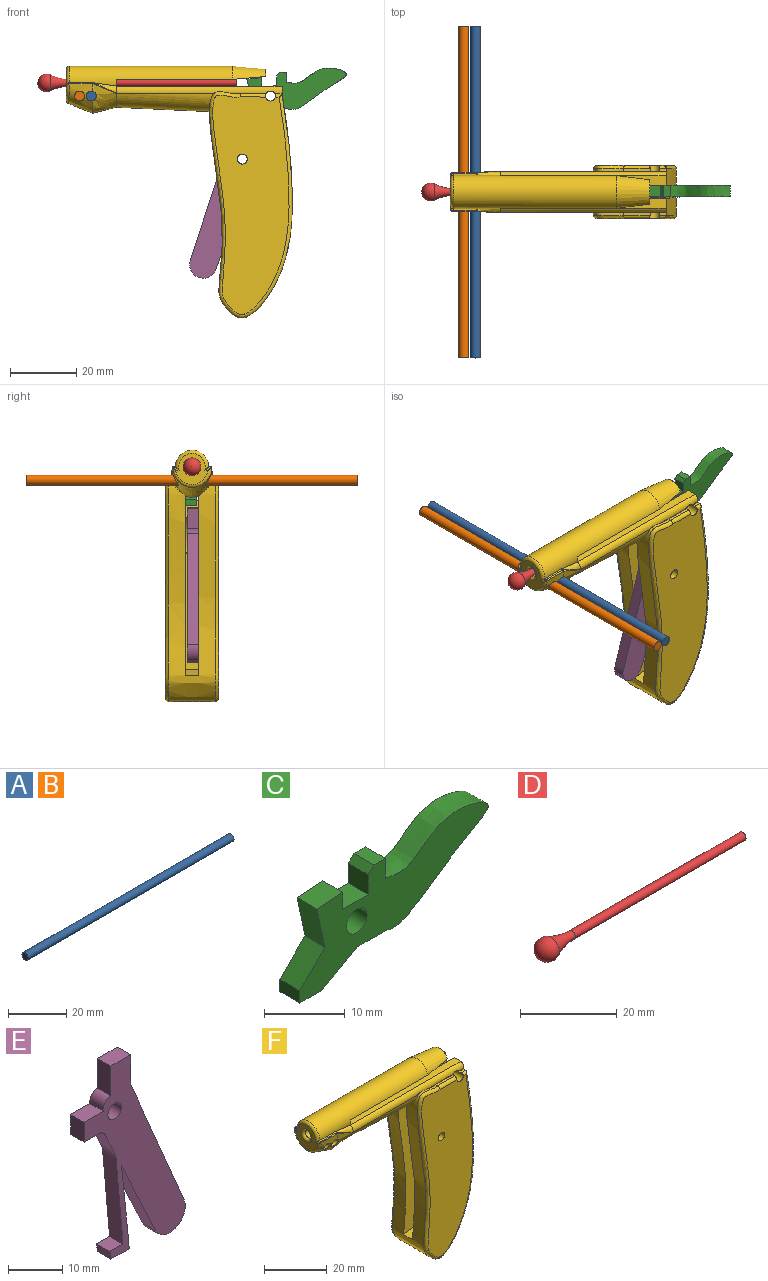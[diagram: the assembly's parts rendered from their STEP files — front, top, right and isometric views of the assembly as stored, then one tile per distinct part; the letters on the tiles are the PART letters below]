
ASSEMBLY  parts=6 mates=5
PART A: 3 faces, bbox 100x3x3 mm
  f0: cylinder r=1.5mm len=100mm, axis (-1,0,0), area 942.5mm2, adj f1,f2
  f1: plane 3x3mm, normal (1,0,0), area 7.1mm2, adj f0
  f2: plane 3x3mm, normal (-1,0,0), area 7.1mm2, adj f0
PART B: same geometry as A
PART C: 17 faces, bbox 33.3x3.5x15.8 mm
  f0: plane 5x3.5mm, normal (0,0,-1), area 17.5mm2, adj f7,f8,f13,f16
  f1: plane 4.5x3.5mm, normal (0,0,1), area 15.8mm2, adj f4,f7,f8,f9
  f2: plane 6.52x3.5mm, normal (-0.98,0,-0.21), area 23.3mm2, adj f5,f7,f8,f12
  f3: plane 3.5x3mm, normal (1,0,0), area 10.5mm2, adj f7,f8,f10,f16
  f4: plane 3.5x2.6mm, normal (1,0,0), area 9.1mm2, adj f1,f5,f7,f8
  f5: plane 4.49x3.5mm, normal (-0.07,0,1), area 15.8mm2, adj f2,f4,f7,f8
  f6: cylinder r=1.8mm len=3.6mm, axis (0,1,0), area 39.6mm2, adj f7,f8
  f7: plane 33.34x15.77mm, normal (0,-1,0), area 226.8mm2, adj f0,f1,f2,f3,f4,f5,f6,f9
  f8: plane 33.04x15.45mm, normal (0,1,0), area 225.1mm2, adj f0,f1,f2,f3,f4,f5,f6,f9
  f9: plane 3.5x3mm, normal (-1,0,0), area 10.5mm2, adj f1,f7,f8,f11
  f10: plane 3.5x2mm, normal (0,0,1), area 7mm2, adj f3,f7,f8,f11
  f11: plane 3.5x1mm, normal (-0.71,0,0.71), area 4.9mm2, adj f7,f8,f9,f10
  f12: plane 4.41x4.41mm, normal (-0.71,0,0.71), area 21.8mm2, adj f2,f7,f8,f15
  f13: plane 6.05x3.5mm, normal (0.5,0,-0.87), area 24.4mm2, adj f0,f7,f8,f14
  f14: plane 3.95x3.5mm, normal (0,0,-1), area 13.8mm2, adj f7,f8,f13,f15
  f15: plane 3.5x1.85mm, normal (-1,0,0), area 6.5mm2, adj f7,f8,f12,f14
  f16: extruded ~18.03x12.17mm, area 142.9mm2, adj f0,f3,f7,f8
PART D: 4 faces, bbox 60x10.8x10.8 mm
  f0: cylinder r=1mm len=50mm, axis (-1,0,0), area 314.2mm2, adj f1,f2
  f1: plane 2x2mm, normal (1,0,0), area 3.1mm2, adj f0
  f2: torus R=14.82mm, axis (1,0,0), area 58.7mm2, adj f0,f3
  f3: sphere r=2.7mm, area 66mm2, adj f2
PART E: 26 faces, bbox 26.5x3.5x45.5 mm
  f0: plane 19.21x8.96mm, normal (-0.91,0,-0.42), area 74.2mm2, adj f9,f10,f16,f20
  f1: plane 3.5x0.5mm, normal (-1,0,0), area 1.8mm2, adj f9,f10,f11,f14
  f2: plane 5.1x3.5mm, normal (-0.91,0,-0.42), area 19.7mm2, adj f9,f10,f15,f25
  f3: plane 3.5x0.13mm, normal (0.39,0,-0.92), area 0.5mm2, adj f9,f10,f16,f17
  f4: plane 32.43x13.67mm, normal (0.92,0,0.39), area 123.2mm2, adj f9,f10,f17,f18
  f5: plane 5.89x3.5mm, normal (1,0,0), area 20.6mm2, adj f6,f9,f10,f18
  f6: plane 5.2x3.5mm, normal (0,0,1), area 18.2mm2, adj f5,f7,f9,f10
  f7: plane 6.7x3.5mm, normal (-1,0,0), area 23.4mm2, adj f6,f9,f10,f14
  f8: cylinder r=1.75mm len=3.5mm, axis (0,1,0), area 38.5mm2, adj f9,f10
  f9: plane 45.48x26.5mm, normal (0,-1,0), area 433.5mm2, adj f0,f1,f2,f3,f4,f5,f6,f7
  f10: plane 45.48x26.5mm, normal (0,1,0), area 433.5mm2, adj f0,f1,f2,f3,f4,f5,f6,f7
  f11: plane 5x3.5mm, normal (0,0,1), area 17.5mm2, adj f1,f9,f10,f13
  f12: plane 3.73x3.5mm, normal (0,0,-1), area 13mm2, adj f9,f10,f13,f15
  f13: plane 4.5x3.5mm, normal (-1,0,0), area 15.8mm2, adj f9,f10,f11,f12
  f14: cylinder r=2mm len=3.5mm, axis (0,1,0), area 11mm2, adj f1,f7,f9,f10
  f15: cylinder r=2mm len=3.5mm, axis (0,-1,0), area 7.9mm2, adj f2,f9,f10,f12
  f16: cylinder r=4mm len=5.18mm, axis (0,1,0), area 21.5mm2, adj f0,f3,f9,f10
  f17: cylinder r=4mm len=5.24mm, axis (0,1,0), area 22mm2, adj f3,f4,f9,f10
  f18: cylinder r=4mm len=3.5mm, axis (0,-1,0), area 5.6mm2, adj f4,f5,f9,f10
  f19: plane 20.31x3.5mm, normal (-1,0,-0.09), area 71.4mm2, adj f9,f10,f24,f25
  f20: plane 18.05x3.5mm, normal (0.99,0,0.1), area 63.5mm2, adj f0,f9,f10,f21
  f21: plane 3.5x1.8mm, normal (1,0,0.07), area 6.3mm2, adj f9,f10,f20,f22
  f22: plane 4.79x3.5mm, normal (-0.02,0,-1), area 16.8mm2, adj f9,f10,f21,f23
  f23: plane 3.5x1.8mm, normal (-0.99,0,-0.13), area 6.4mm2, adj f9,f10,f22,f24
  f24: plane 3.5x3.41mm, normal (0,0,1), area 11.9mm2, adj f9,f10,f19,f23
  f25: cylinder r=5mm len=3.5mm, axis (0,1,0), area 6.1mm2, adj f2,f9,f10,f19
PART F: 81 faces, bbox 68.3x16.1x76.4 mm
  f0: plane 6.97x5.07mm, normal (-0.59,0,0.81), area 34.5mm2, adj f1,f33,f34,f51
  f1: extruded ~68.03x24.91mm, area 1736.4mm2, adj f0,f3,f4,f10,f11,f12,f13,f14
  f2: cylinder r=1.5mm len=6mm, axis (0,-1,0), area 49.7mm2, adj f4,f5,f27,f34,f42,f43,f44,f46
  f3: bspline ~35x2.96mm, area 0mm2, adj f1,f19,f27
  f4: extruded ~2.24x0.24mm, area 0.4mm2, adj f1,f2,f20,f27,f43
  f5: extruded ~7.96x0.14mm, area 0.5mm2, adj f2,f27,f42
  f6: cylinder r=1.5mm len=6mm, axis (0,1,0), area 56.5mm2, adj f33,f37
  f7: cylinder r=1.5mm len=6mm, axis (0,-1,0), area 49.7mm2, adj f9,f11,f12,f33,f35,f36,f37,f38
  f8: plane 7.88x4mm, normal (1,0,0), area 30.7mm2, adj f16,f17,f18,f33,f34,f49
  f9: extruded ~7.96x0.14mm, area 0.5mm2, adj f7,f12,f35
  f10: extruded ~2.28x0.17mm, area 0.3mm2, adj f1,f12,f13
  f11: extruded ~2.24x0.24mm, area 0.4mm2, adj f1,f7,f12,f15,f36
  f12: cylinder r=2mm len=50mm, axis (1,0,0), area 131.6mm2, adj f1,f7,f9,f10,f11,f13,f14,f15
  f13: bspline ~35x2.96mm, area 0mm2, adj f1,f10,f12
  f14: bspline ~35x12.17mm, area 477.7mm2, adj f1,f12,f27,f56,f72,f78
  f15: plane 4.12x2.43mm, normal (1,0,0), area 9.4mm2, adj f1,f11,f12,f17,f33
  f16: cylinder r=1.5mm len=49mm, axis (-1,0,0), area 308.6mm2, adj f8,f17,f18,f23,f24,f25,f26,f31
  f17: plane 50x3.78mm, normal (0,0,1), area 175.8mm2, adj f8,f12,f15,f16,f23,f33
  f18: plane 50x3.78mm, normal (0,0,1), area 175.8mm2, adj f8,f16,f20,f25,f27,f34
  f19: extruded ~2.28x0.17mm, area 0.3mm2, adj f1,f3,f27
  f20: plane 4.12x2.43mm, normal (1,0,0), area 9.4mm2, adj f1,f4,f18,f27,f34
  f21: cylinder r=5mm len=49mm, axis (-1,0,0), area 706.3mm2, adj f23,f24,f25,f26,f29,f54,f55,f57
  f22: plane 9.83x9.32mm, normal (-1,0,0), area 45.3mm2, adj f60,f61,f62,f63,f66
  f23: plane 3.88x2mm, normal (1,0,0), area 7.2mm2, adj f16,f17,f21,f24
  f24: plane 35x3.78mm, normal (0,0,-1), area 132.3mm2, adj f16,f21,f23,f30
  f25: plane 3.88x2mm, normal (1,0,0), area 7.2mm2, adj f16,f18,f21,f26
  f26: plane 35x3.78mm, normal (0,0,-1), area 132.3mm2, adj f16,f21,f25,f28
  f27: cylinder r=2mm len=50mm, axis (-1,0,0), area 131.6mm2, adj f1,f2,f3,f4,f5,f14,f18,f19
  f28: plane 10.15x3.93mm, normal (0.09,0,-1), area 30.3mm2, adj f26,f29,f31,f32
  f29: cone r=5mm half-angle=5deg, axis (-1,0,0), area 113.4mm2, adj f21,f28,f30,f32
  f30: plane 10.15x3.93mm, normal (0.09,0,-1), area 30.3mm2, adj f24,f29,f31,f32
  f31: cone r=1.5mm half-angle=5deg, axis (1,0,0), area 28.9mm2, adj f16,f28,f30,f32
  f32: plane 7.35x2.25mm, normal (1,0,0), area 10.8mm2, adj f28,f29,f30,f31
  f33: plane 62.43x23.55mm, normal (0,1,0), area 825.1mm2, adj f0,f1,f6,f7,f8,f15,f17,f41
  f34: plane 62.43x23.55mm, normal (0,-1,0), area 825.1mm2, adj f0,f1,f2,f8,f18,f20,f41,f45
  f35: plane 7.88x0.92mm, normal (0.02,0,1), area 7.2mm2, adj f1,f7,f9,f38
  f36: plane 2.14x0.93mm, normal (0.02,0,1), area 2mm2, adj f1,f7,f11,f40
  f37: plane 66.12x23.01mm, normal (0,-1,0), area 1183.2mm2, adj f6,f7,f38,f39,f40
  f38: cylinder r=1mm len=7.9mm, axis (1,0,-0.02), area 12.2mm2, adj f7,f35,f37,f39
  f39: bspline ~68.87x25.01mm, area 235.8mm2, adj f1,f37,f38,f40
  f40: cylinder r=1mm len=2.15mm, axis (1,0,-0.02), area 2.6mm2, adj f7,f36,f37,f39
  f41: plane 4x3.9mm, normal (-0.05,0,-1), area 15.6mm2, adj f1,f33,f34,f49
  f42: plane 7.88x0.92mm, normal (0.02,0,1), area 7.2mm2, adj f1,f2,f5,f46
  f43: plane 2.14x0.93mm, normal (0.02,0,1), area 2mm2, adj f1,f2,f4,f48
  f44: plane 66.12x23.01mm, normal (0,1,0), area 1183.1mm2, adj f2,f45,f46,f47,f48
  f45: cylinder r=1.5mm len=6mm, axis (0,1,0), area 56.5mm2, adj f34,f44
  f46: cylinder r=1mm len=7.9mm, axis (-1,0,0.02), area 12.2mm2, adj f2,f42,f44,f47
  f47: bspline ~68.88x25.01mm, area 235.9mm2, adj f1,f44,f46,f48
  f48: cylinder r=1mm len=2.15mm, axis (-1,0,0.02), area 2.6mm2, adj f2,f43,f44,f47
  f49: plane 4x3mm, normal (0,0,-1), area 12mm2, adj f8,f33,f34,f41
  f50: plane 4.22x4mm, normal (-0.01,0,1), area 16.9mm2, adj f33,f34,f51,f53
  f51: cylinder r=9.32mm len=10.8mm, axis (0,-1,0), area 49.1mm2, adj f0,f33,f34,f50
  f52: plane 10.54x4mm, normal (-0.16,0,0.99), area 42.7mm2, adj f1,f33,f34,f53
  f53: plane 35.08x4mm, normal (-1,0,0.06), area 140.5mm2, adj f33,f34,f50,f52
  f54: bspline ~6.93x3.14mm, area 10.4mm2, adj f12,f21,f65,f72
  f55: bspline ~6.93x3.14mm, area 10.4mm2, adj f21,f27,f64,f78
  f56: bspline ~12.17x9.22mm, area 134mm2, adj f14,f58,f71,f72,f77,f78,f79
  f57: plane 6.93x0.7mm, normal (0,0,1), area 4.8mm2, adj f21,f63,f64,f75
  f58: bspline ~12x9.22mm, area 128.4mm2, adj f56,f61,f68,f69,f70,f74,f75,f76
  f59: plane 6.93x0.7mm, normal (0,0,1), area 4.8mm2, adj f21,f60,f65,f69
  f60: cylinder r=1mm len=1.82mm, axis (0,1,0), area 1.3mm2, adj f22,f59,f62,f67,f68
  f61: bspline ~12x6.23mm, area 23mm2, adj f22,f58,f67,f73
  f62: torus R=4mm, axis (1,0,0), area 24.7mm2, adj f21,f22,f60,f63
  f63: cylinder r=1mm len=1.82mm, axis (0,1,0), area 1.3mm2, adj f22,f57,f62,f73,f74
  f64: bspline ~0.95x0.37mm, area 0.2mm2, adj f21,f55,f57,f76,f77
  f65: bspline ~0.95x0.37mm, area 0.2mm2, adj f21,f54,f59,f70,f71
  f66: torus R=2.5mm, axis (1,0,0), area 18.4mm2, adj f16,f22
  f67: bspline ~1.18x1.1mm, area 0.4mm2, adj f60,f61,f68
  f68: bspline ~0.38x0.33mm, area 0mm2, adj f58,f60,f67,f69
  f69: bspline ~9.22x0.32mm, area 3.3mm2, adj f58,f59,f68,f70
  f70: bspline ~0.69x0.38mm, area 0.1mm2, adj f58,f65,f69,f71
  f71: bspline ~0.45x0.39mm, area 0mm2, adj f56,f65,f70,f72
  f72: bspline ~9.42x4.26mm, area 1.3mm2, adj f12,f14,f54,f56,f71
  f73: bspline ~1.18x1.1mm, area 0.4mm2, adj f61,f63,f74
  f74: bspline ~0.38x0.33mm, area 0mm2, adj f58,f63,f73,f75
  f75: bspline ~9.22x0.32mm, area 3.3mm2, adj f57,f58,f74,f76
  f76: bspline ~0.68x0.38mm, area 0.1mm2, adj f58,f64,f75,f77
  f77: bspline ~0.45x0.38mm, area 0mm2, adj f56,f64,f76,f78
  f78: bspline ~9.67x4.37mm, area 1.3mm2, adj f14,f27,f55,f56,f77
  f79: cylinder r=1.5mm len=11.52mm, axis (0,-1,0), area 100.1mm2, adj f56,f58
  f80: cylinder r=1.5mm len=8.18mm, axis (0,-1,0), area 77.1mm2, adj f58
PLACE A rot(axis=(0,0,1),90deg) t=(7.3,0,-1.33)mm
PLACE B rot(axis=(0,0,1),90deg) t=(3.8,0,-1.33)mm
PLACE C rot(axis=(0,-1,0),1.5deg) t=(-0.28,0.4,1.1)mm
PLACE D t=(1.13,0,2.67)mm
PLACE E rot(axis=(-0.04,0,1),180deg) t=(55.45,-0.4,-16.09)mm
PLACE F t=(-0.2,0,2.67)mm fixed
MATE slider F.f16 <-> D.f0  axis (-1,0,0) through (0.8,0,2.67)mm
MATE fastened A.f0 <-> F.f79  axis (0,-1,0) through (7.3,0,-1.33)mm
MATE revolute F.f6 <-> E.f8  axis (0,1,0) through (52.8,-2,-20.33)mm
MATE revolute C.f6 <-> F.f2  axis (0,1,0) through (61.3,2,-1.33)mm
MATE fastened B.f0 <-> F.f80  axis (0,-1,0) through (3.8,0,-1.33)mm
